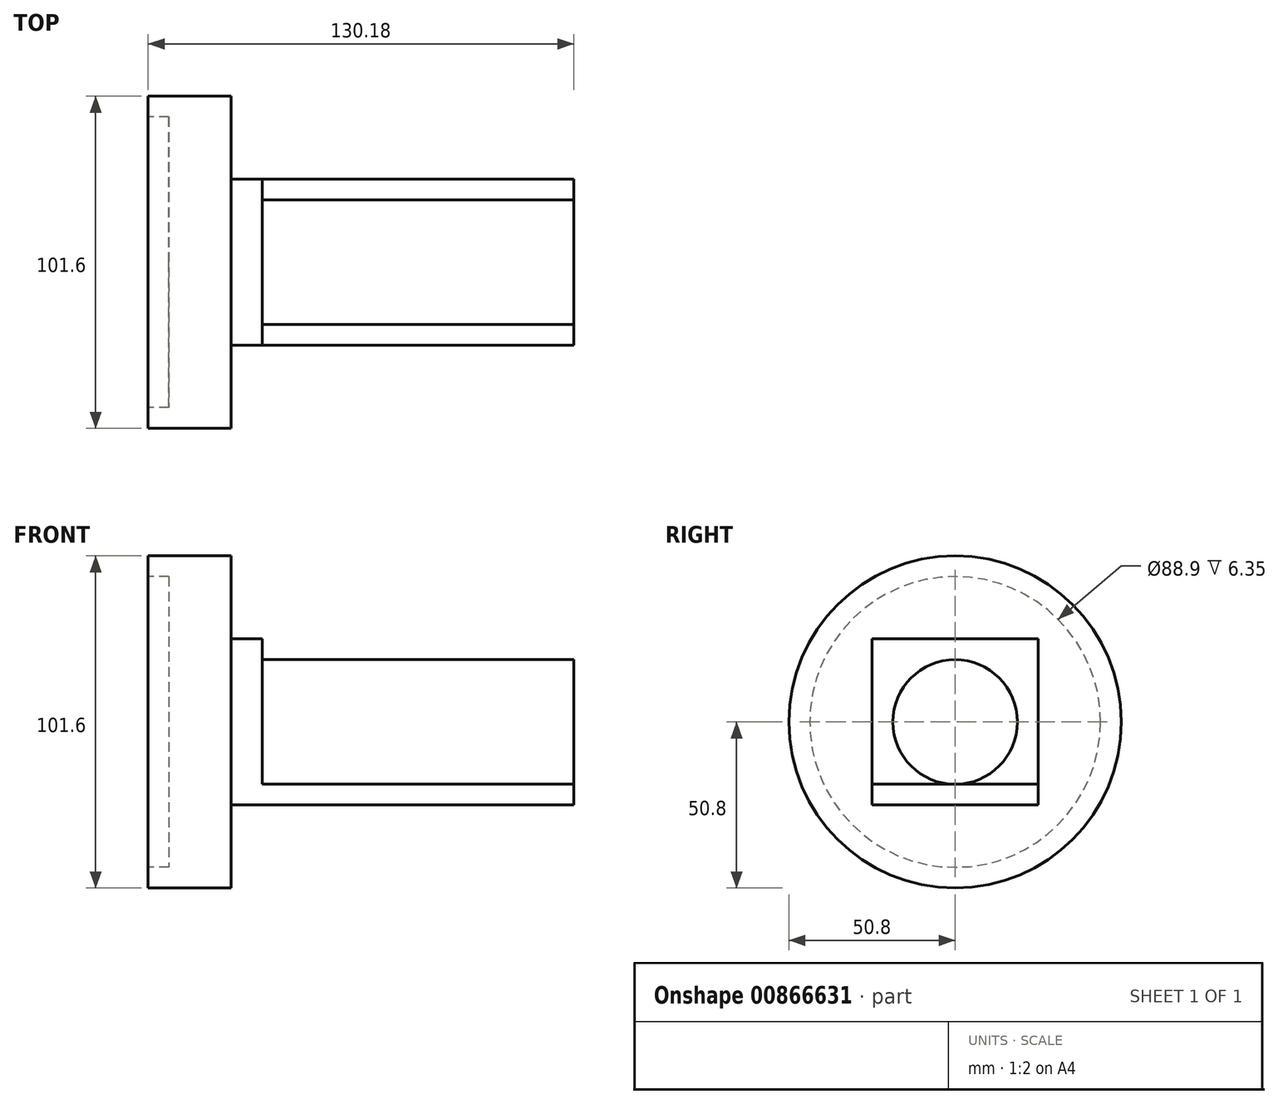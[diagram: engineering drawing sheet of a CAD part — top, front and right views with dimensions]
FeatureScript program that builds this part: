
annotation { "Feature Type Name" : "Feature", "Feature Type Description" : "" }
export const myFeature = defineFeature(function(context is Context, id is Id, definition is map)
    precondition{}
    {
        {
            var Q0;
            Q0=qCreatedBy(makeId("Top.planeOp"),FACE);
            var sketch = newSketch(context, id + "F0", { "sketchPlane" : qUnion([Q0])});
            skLineSegment(sketch, "E0.bottom", {"start": v(0, 0) * mm, "end": v(9.52, 0) * mm});
            skLineSegment(sketch, "E0.top", {"start": v(0, -50.8) * mm, "end": v(9.53, -50.8) * mm});
            skLineSegment(sketch, "E0.left", {"start": v(0, 0) * mm, "end": v(0, -50.8) * mm});
            skLineSegment(sketch, "E0.right", {"start": v(9.53, 0) * mm, "end": v(9.53, -50.8) * mm});
            skSolve(sketch);
        }
        {
            var Q0;
            Q0 = qSketchRegion(id + "F0", true);
            extrude(context, id + "F1", {"entities" : qUnion([Q0]), "depth" : 50.8 * mm, "offsetDistance" : 25.4 * mm});
        }
        {
            var Q0;
            Q0=makeQuery(id+"F1.opExtrude","SWEPT_FACE",FACE,{"disambiguationData":[OSD([sQuery(id+"F0.wireOp",EDGE,"E0.right")])]});
            var sketch = newSketch(context, id + "F2", { "sketchPlane" : qUnion([Q0])});
            skLineSegment(sketch, "E1.bottom", {"start": v(-50.8, 0) * mm, "end": v(0, 0) * mm});
            skLineSegment(sketch, "E1.top", {"start": v(-50.8, 6.35) * mm, "end": v(0, 6.35) * mm});
            skLineSegment(sketch, "E1.left", {"start": v(-50.8, 0) * mm, "end": v(-50.8, 6.35) * mm});
            skLineSegment(sketch, "E1.right", {"start": v(0, 0) * mm, "end": v(0, 6.35) * mm});
            skSolve(sketch);
        }
        {
            var Q0;
            Q0=makeQuery(id+"F2.imprint","IMPRINT",FACE,{"disambiguationData":[TD([[makeQuery(id+"F2.imprint","IMPRINT",EDGE,{"derivedFrom":sQuery(id+"F2.wireOp",EDGE,"E1.bottom")}),-1.0]])]});
            extrude(context, id + "F3", {"entities" : qUnion([Q0]), "operationType" : NewBodyOperationType.ADD, "depth" : 95.25 * mm, "offsetDistance" : 25.4 * mm});
        }
        {
            var Q0;
            Q0=makeQuery(id+"F1.opExtrude","SWEPT_FACE",FACE,{"disambiguationData":[OSD([sQuery(id+"F0.wireOp",EDGE,"E0.left")])]});
            var sketch = newSketch(context, id + "F4", { "sketchPlane" : qUnion([Q0])});
            skLineSegment(sketch, "E2", {"start": v(0, 25.4) * mm, "end": v(25.4, 25.4) * mm});
            skCircle(sketch, "E3", {"center": v(25.4, 25.4) * mm, "radius": 44.45 * mm});
            skCircle(sketch, "E4", {"center": v(25.4, 25.4) * mm, "radius": 50.8 * mm});
            skSolve(sketch);
        }
        {
            var Q0;
            Q0=makeQuery(id+"F4.imprint","IMPRINT",FACE,{"disambiguationData":[TD([[makeQuery(id+"F4.imprint","IMPRINT",EDGE,{"derivedFrom":sQuery(id+"F4.wireOp",EDGE,"E3")}),1.0]])]});
            var Q1;
            {var subQ0=sQuery(id+"F0.wireOp",EDGE,"E0.left");var subQ1=makeQuery(id+"F1.opExtrude","CAP_EDGE",EDGE,{"disambiguationData":[OSD([subQ0])],"isStart":true});Q1=makeQuery(id+"F4.imprint","IMPRINT",FACE,{"disambiguationData":[TD([[makeQuery(id+"F4.imprint","IMPRINT",EDGE,{"derivedFrom":subQ1}),1.0]])]});}
            var Q2;
            Q2=makeQuery(id+"F4.imprint","IMPRINT",FACE,{"disambiguationData":[TD([[makeQuery(id+"F4.imprint","IMPRINT",EDGE,{"derivedFrom":sQuery(id+"F4.wireOp",EDGE,"E3")}),-1.0]])]});
            extrude(context, id + "F5", {"entities" : qUnion([Q0, Q1, Q2]), "operationType" : NewBodyOperationType.ADD, "depth" : 25.4 * mm, "offsetDistance" : 25.4 * mm});
        }
        {
            var Q0;
            Q0=makeQuery(id+"F5.opExtrude","CAP_FACE",FACE,{"disambiguationData":[OSD([sQuery(id+"F4.wireOp",EDGE,"E4")])],"isStart":false});
            var sketch = newSketch(context, id + "F6", { "sketchPlane" : qUnion([Q0])});
            skCircle(sketch, "E5", {"center": v(25.4, 25.4) * mm, "radius": 44.45 * mm});
            skSolve(sketch);
        }
        {
            var Q0;
            Q0=makeQuery(id+"F6.imprint","IMPRINT",FACE,{"disambiguationData":[TD([[makeQuery(id+"F6.imprint","IMPRINT",EDGE,{"derivedFrom":sQuery(id+"F6.wireOp",EDGE,"E5")}),1.0]])]});
            extrude(context, id + "F7", {"entities" : qUnion([Q0]), "operationType" : NewBodyOperationType.REMOVE, "oppositeDirection" : true, "depth" : 6.35 * mm, "offsetDistance" : 25.4 * mm});
        }
        {
            var Q0;
            Q0=makeQuery(id+"F1.opExtrude","SWEPT_FACE",FACE,{"disambiguationData":[OSD([sQuery(id+"F0.wireOp",EDGE,"E0.right")])]});
            var sketch = newSketch(context, id + "F8", { "sketchPlane" : qUnion([Q0])});
            skLineSegment(sketch, "E6", {"start": v(-25.4, 50.8) * mm, "end": v(-25.4, 25.4) * mm});
            skCircle(sketch, "E7", {"center": v(-25.4, 25.4) * mm, "radius": 19.05 * mm});
            skSolve(sketch);
        }
        {
            var Q0;
            {var subQ0=sQuery(id+"F8.wireOp",EDGE,"E7");var subQ1=makeQuery(id+"F8.imprint","INTERSECT",VERTEX,{"derivedFrom":[sQuery(id+"F8.wireOp",EDGE,"E6"),subQ0]});Q0=makeQuery(id+"F8.imprint","IMPRINT",FACE,{"disambiguationData":[TD([[makeQuery(id+"F8.imprint","IMPRINT",EDGE,{"disambiguationData":[TD([[subQ1,-1.0]])],"derivedFrom":subQ0}),1.0]])]});}
            extrude(context, id + "F9", {"entities" : qUnion([Q0]), "depth" : 95.25 * mm, "offsetDistance" : 25.4 * mm});
        }
    });
